# Revit family: 4462_Addressable Dual Input Unit
name_source: partatom
category: Fire Alarm Devices
units: mm (PartAtom-declared; Revit-internal decimal feet)

## family parameters
Cut with Voids When Loaded = No
Host = Face
Maintain Annotation Orientation = No
OmniClass Number = 23.85.30.21
OmniClass Title = Environmental Detection/Registration
Part Type = Normal
Room Calculation Point = No
Round Connector Dimension = Use Diameter
Shared = No

## types (1)
- 4462
    Ambient Humidity = Maximum 95 % RH
    Ambient Temperature Operating = -10 to +50 °C
    Ambient Temperature Storage = -20 to +60 °C
    CPR = 0786-CPR-21589
    Current (Active) = ≤ 2.2 mA
    Current Quiescent = ≤ 2.2 mA
    Default Elevation = 0 mm  [stored 0 ft]
    Depth (mm) = 49 mm  [stored 0.160761 ft]
    Description = Addressable 2 inputs unit with isolator 4462
    Enclosure = Standard Fibox encapsulation. (JB 6 G)
    General Inputs = 2
    Height (mm) = 110 mm  [stored 0.360892 ft]
    Ingress Protection Rating = IP65
    Manufacturer = Panasonic
    Max_Wire Size = Ø 1.2 mm (1.5 mm²)
    Min_Wire Size = Ø 0.6 mm (0.28 mm²)
    Model = 4462
    Omniclass Code = 23.85.30.21.11.11.11
    Omniclass Description = Smoke Detectors
    Power Supply = Via COM loop
    Product Material = Polycarbonate_Panasonic_White
    Relay Outputs = 2
    Short Circuit Isolator = Yes (Built-in)
    Tested and Approved = EN54-18, EN54-17
    Type Comments = The 4462 is a dual input unit with isolator for monitoring of various equipment like switches, sprinkler valves, etc. The inputs are programmed via EBLWin. NC or NO contact.
    URL = https://www.panasonic-fire-security.com
    Uniclass 2015 Code = Pr_75_80_30_27
    Uniclass 2015 Description = Fire and smoke detector bases
    Uniformat 2010  Code = D7050
    Uniformat 2010 Description = Detection and Alarm
    Vds Approval = G218081
    Version = RVT20
    Voltage Allowed = 12 – 30 VDC
    Voltage Normal = 24 VDC
    Weight = 188g
    Width (mm) = 110 mm  [stored 0.360892 ft]

note: [stored X ft] marks values corroborated as IEEE doubles in the binary element streams (Revit-internal decimal feet)

## geometry (parser evidence)
native form markers: Blend x86, Sweep x2
no freeform markers — native parametric forms only
